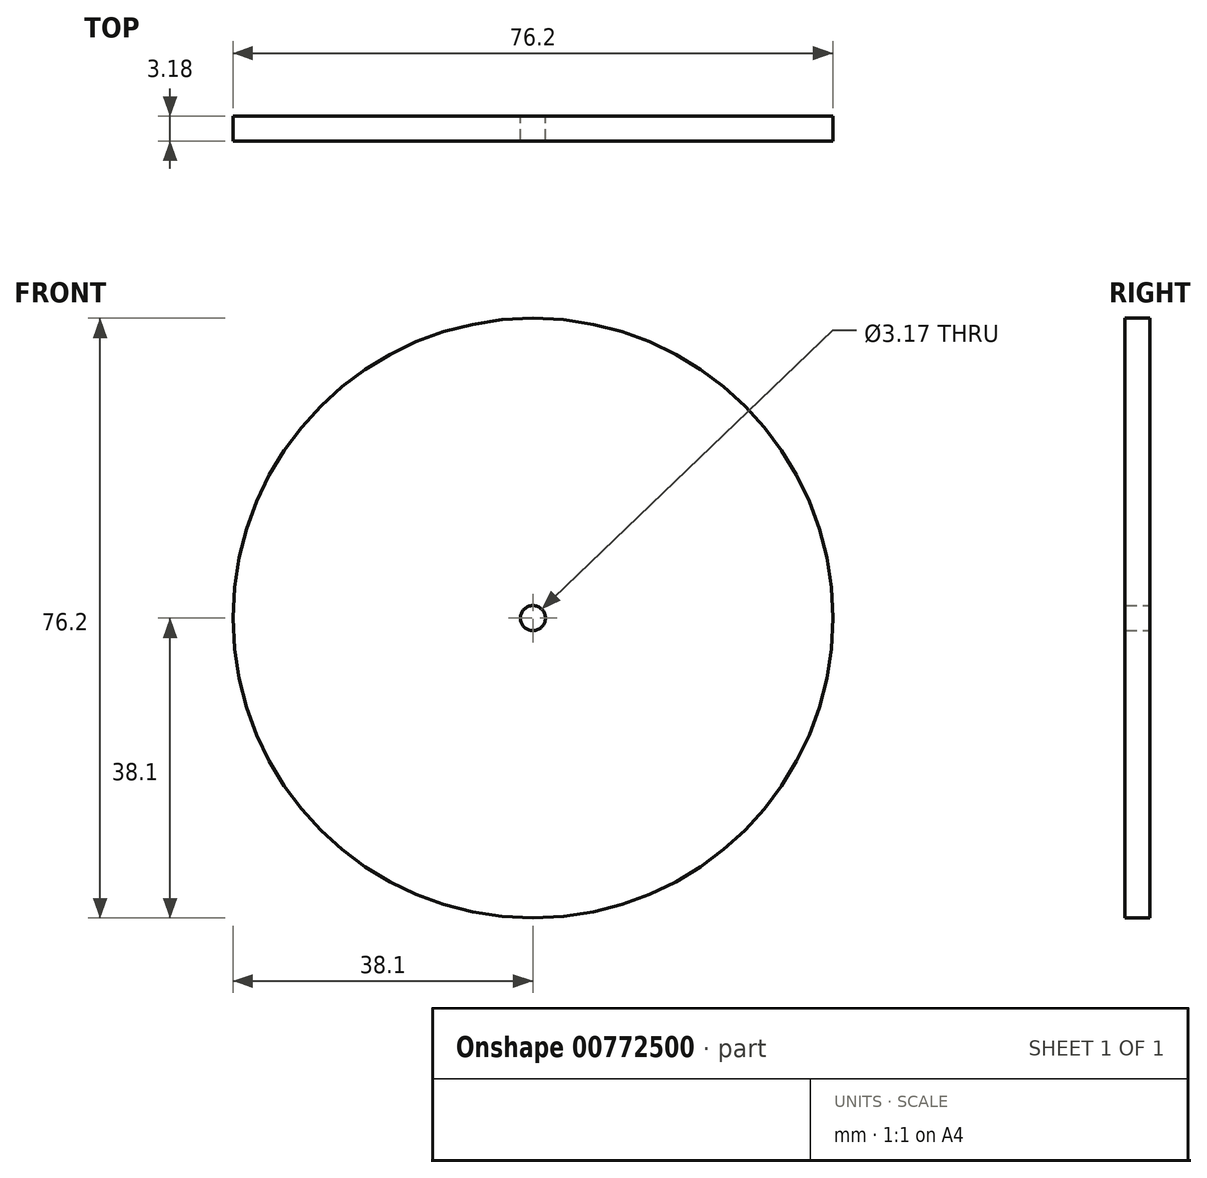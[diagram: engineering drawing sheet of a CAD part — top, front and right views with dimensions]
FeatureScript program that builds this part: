
annotation { "Feature Type Name" : "Feature", "Feature Type Description" : "" }
export const myFeature = defineFeature(function(context is Context, id is Id, definition is map)
    precondition{}
    {
        {
            var Q0;
            Q0=qCreatedBy(makeId("Front.planeOp"),FACE);
            var sketch = newSketch(context, id + "F0", { "sketchPlane" : qUnion([Q0])});
            skCircle(sketch, "E0", {"center": v(0, 0) * mm, "radius": 38.1 * mm});
            skCircle(sketch, "E1", {"center": v(0, 0) * mm, "radius": 1.59 * mm});
            skSolve(sketch);
        }
        {
            var Q0;
            Q0=makeQuery(id+"F0.imprint","IMPRINT",FACE,{"disambiguationData":[TD([[makeQuery(id+"F0.imprint","IMPRINT",EDGE,{"derivedFrom":sQuery(id+"F0.wireOp",EDGE,"E0")}),1.0]])]});
            extrude(context, id + "F1", {"entities" : qUnion([Q0]), "depth" : 3.17 * mm, "offsetDistance" : 25.4 * mm});
        }
    });
